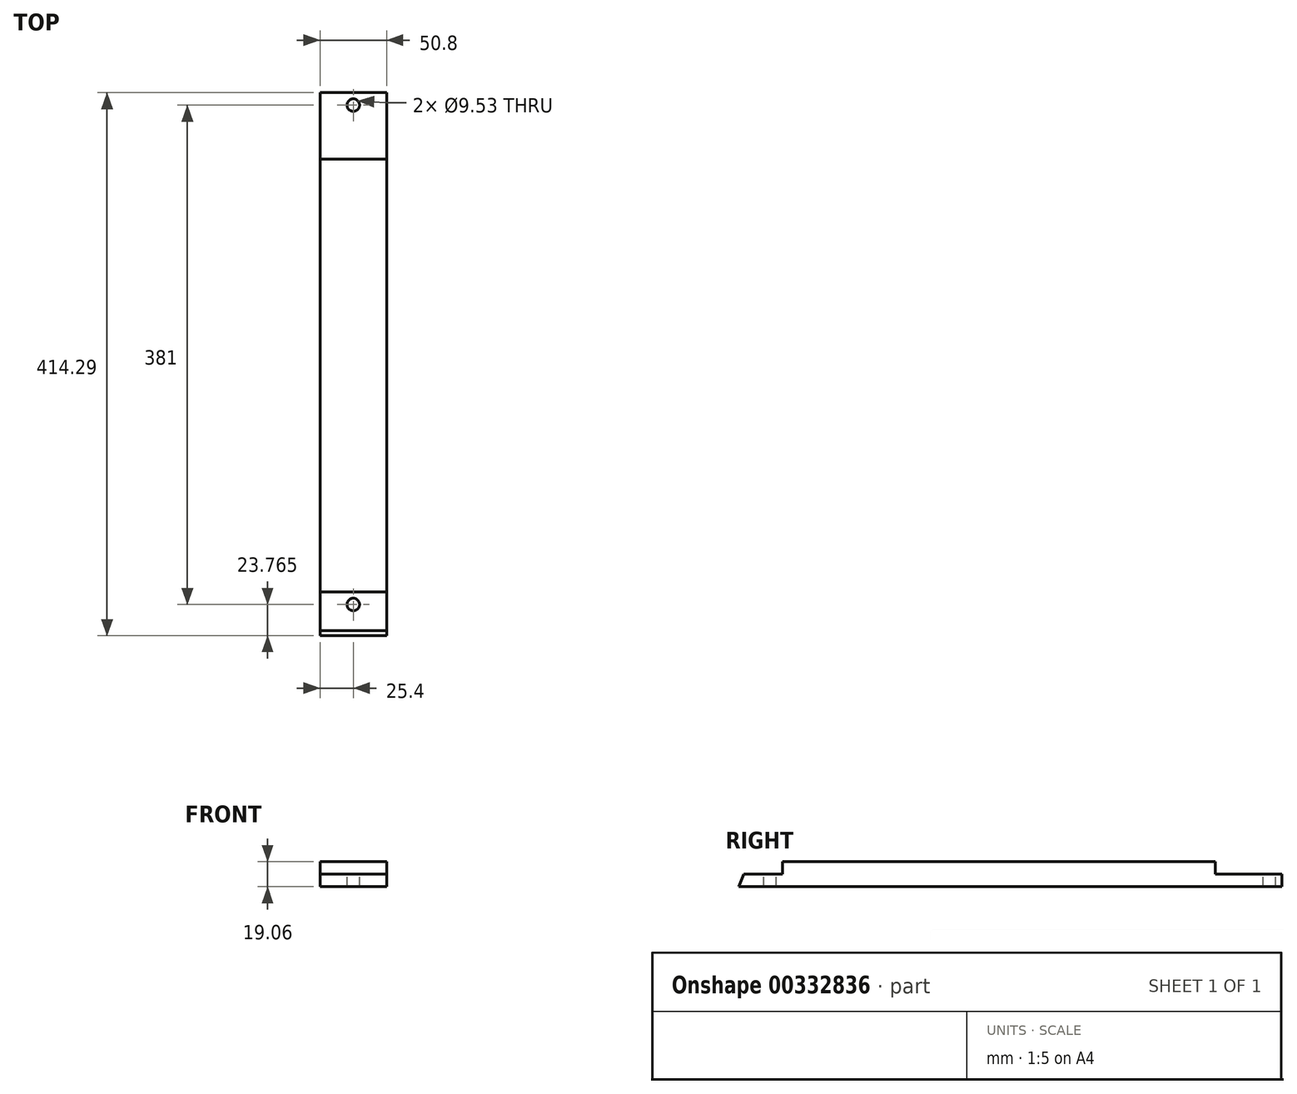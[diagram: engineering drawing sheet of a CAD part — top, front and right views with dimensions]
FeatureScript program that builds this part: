
annotation { "Feature Type Name" : "Feature", "Feature Type Description" : "" }
export const myFeature = defineFeature(function(context is Context, id is Id, definition is map)
    precondition{}
    {
        {
            var Q0;
            Q0=qCreatedBy(makeId("Right.planeOp"),FACE);
            var sketch = newSketch(context, id + "F0", { "sketchPlane" : qUnion([Q0])});
            skLineSegment(sketch, "E0.right", {"start": v(0, 9.52) * mm, "end": v(330.2, 9.53) * mm});
            skLineSegment(sketch, "E1.top", {"start": v(0, 9.52) * mm, "end": v(0, 0) * mm});
            skLineSegment(sketch, "E1.right", {"start": v(-29.35, 0) * mm, "end": v(0, 0) * mm});
            skLineSegment(sketch, "E2", {"start": v(-29.35, 0) * mm, "end": v(-33.3, -9.53) * mm});
            skLineSegment(sketch, "E3", {"start": v(381, -9.52) * mm, "end": v(-33.3, -9.53) * mm});
            skLineSegment(sketch, "E4.bottom", {"start": v(381, 0) * mm, "end": v(381, -9.52) * mm});
            skLineSegment(sketch, "E4.top", {"start": v(330.2, 9.53) * mm, "end": v(330.2, 0) * mm});
            skLineSegment(sketch, "E4.right", {"start": v(381, 0) * mm, "end": v(330.2, 0) * mm});
            skLineSegment(sketch, "E5", {"start": v(0, 9.52) * mm, "end": v(-25.4, 9.52) * mm, "construction": true});
            skLineSegment(sketch, "E6", {"start": v(-29.35, 0) * mm, "end": v(-25.4, 9.52) * mm, "construction": true});
            skSolve(sketch);
        }
        {
            var Q0;
            Q0=qSketchRegion(id+"F0",true);
            extrude(context, id + "F1", {"entities" : qUnion([Q0]), "endBound" : BoundingType.SYMMETRIC, "depth" : 50.8 * mm});
        }
        {
            var Q0;
            Q0=qCreatedBy(makeId("Top.planeOp"),FACE);
            var sketch = newSketch(context, id + "F2", { "sketchPlane" : qUnion([Q0])});
            skCircle(sketch, "E7", {"center": v(0, -9.53) * mm, "radius": 4.76 * mm});
            skCircle(sketch, "E8", {"center": v(0, 371.47) * mm, "radius": 4.76 * mm});
            skSolve(sketch);
        }
        {
            var Q0;
            Q0 = qSketchRegion(id + "F2", true);
            extrude(context, id + "F3", {"entities" : qUnion([Q0]), "operationType" : NewBodyOperationType.REMOVE, "oppositeDirection" : true, "depth" : 25.4 * mm});
        }
    });
